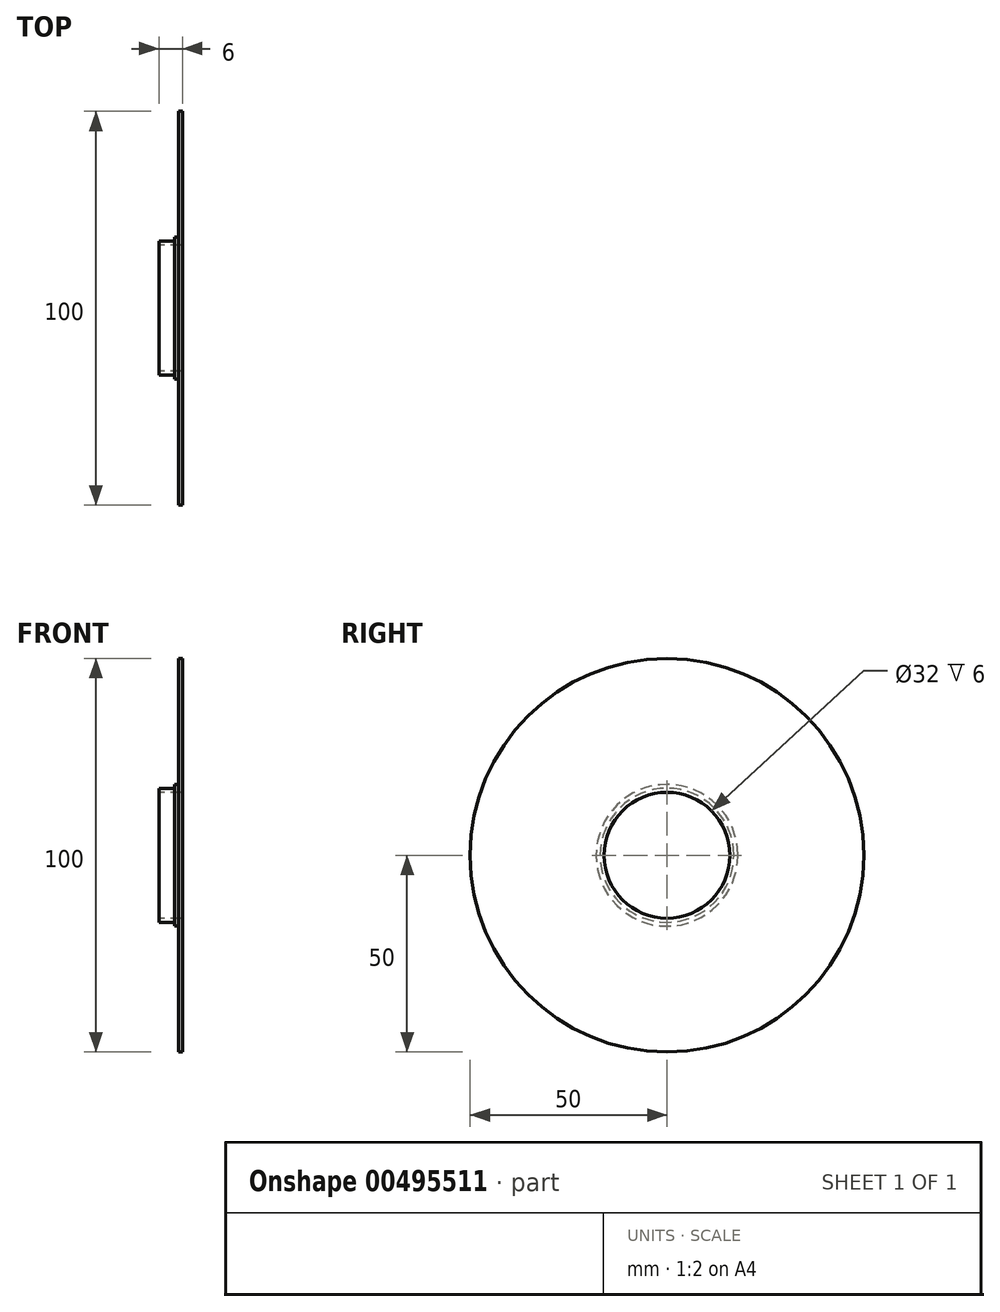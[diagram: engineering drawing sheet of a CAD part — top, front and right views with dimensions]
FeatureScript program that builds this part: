
annotation { "Feature Type Name" : "Feature", "Feature Type Description" : "" }
export const myFeature = defineFeature(function(context is Context, id is Id, definition is map)
    precondition{}
    {
        {
            var Q0;
            Q0=qCreatedBy(makeId("Front.planeOp"),FACE);
            var sketch = newSketch(context, id + "F0", { "sketchPlane" : qUnion([Q0])});
            skLineSegment(sketch, "E0", {"start": v(19.28, 0) * mm, "end": v(42.08, 0) * mm, "construction": true});
            skLineSegment(sketch, "E1.bottom", {"start": v(-25, 50) * mm, "end": v(-24, 50) * mm});
            skLineSegment(sketch, "E1.left", {"start": v(-25, 50) * mm, "end": v(-25, 18) * mm});
            skLineSegment(sketch, "E1.right", {"start": v(-24, 50) * mm, "end": v(-24, 16) * mm});
            skLineSegment(sketch, "E2.bottom", {"start": v(-25, 18) * mm, "end": v(-26, 18) * mm});
            skLineSegment(sketch, "E2.right", {"start": v(-26, 18) * mm, "end": v(-26, 17) * mm});
            skLineSegment(sketch, "E3.top", {"start": v(-26, 17) * mm, "end": v(-30, 17) * mm});
            skLineSegment(sketch, "E3.right", {"start": v(-30, 16) * mm, "end": v(-30, 17) * mm});
            skLineSegment(sketch, "E4", {"start": v(-30, 16) * mm, "end": v(-24, 16) * mm});
            skSolve(sketch);
        }
        {
            var Q0;
            Q0=makeQuery(id+"F0.imprint","IMPRINT",FACE,{"disambiguationData":[TD([[makeQuery(id+"F0.imprint","IMPRINT",EDGE,{"derivedFrom":sQuery(id+"F0.wireOp",EDGE,"E1.bottom")}),-1.0]])]});
            var Q1;
            Q1=sQuery(id+"F0.wireOp",EDGE,"E0");
            revolve(context, id + "F1", {"entities" : qUnion([Q0]), "axis" : qUnion([Q1]), "revolveType" : RevolveType.FULL});
        }
    });
